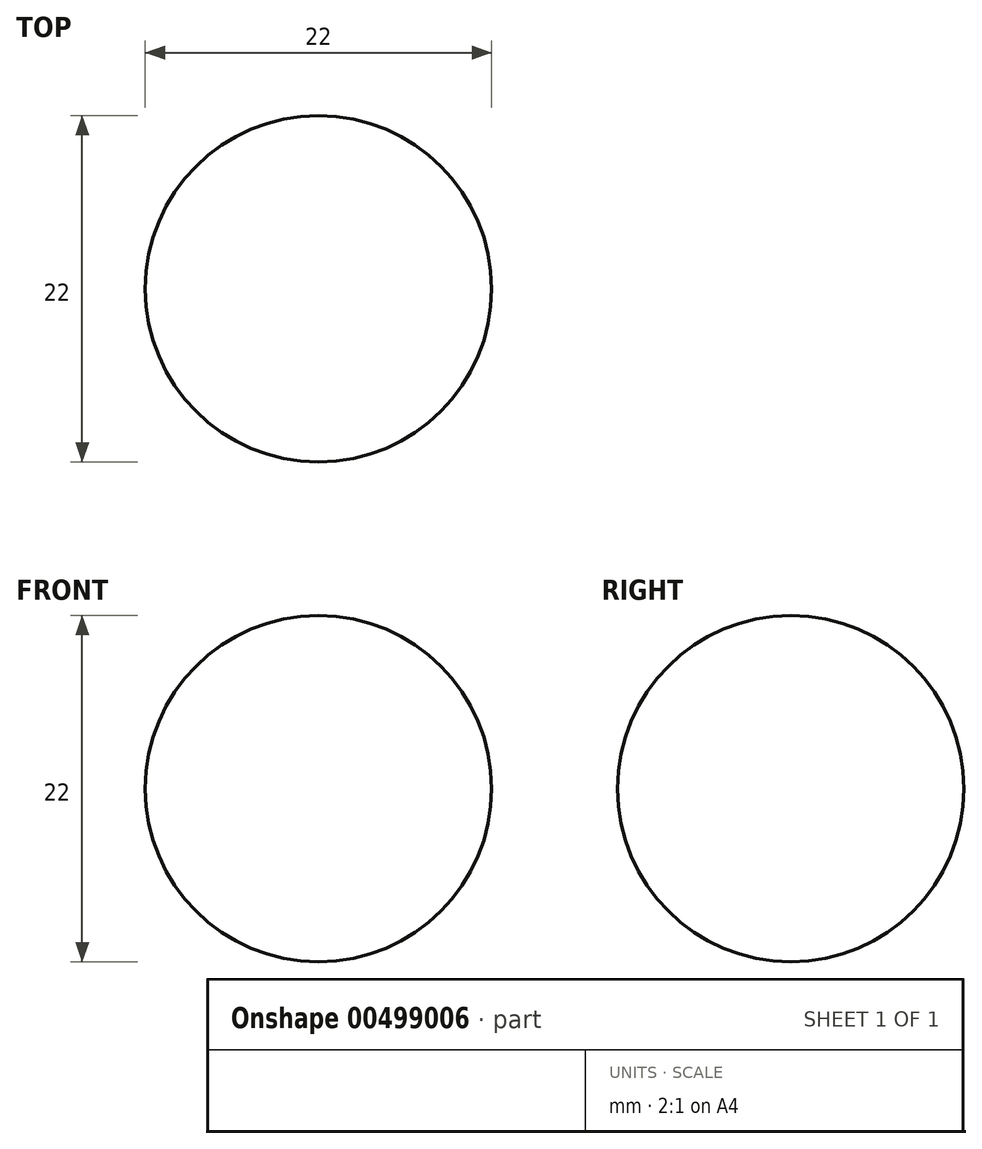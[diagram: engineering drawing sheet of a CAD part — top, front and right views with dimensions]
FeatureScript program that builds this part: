
annotation { "Feature Type Name" : "Feature", "Feature Type Description" : "" }
export const myFeature = defineFeature(function(context is Context, id is Id, definition is map)
    precondition{}
    {
        {
            var Q0;
            Q0=qCreatedBy(makeId("Top.planeOp"),FACE);
            var sketch = newSketch(context, id + "F0", { "sketchPlane" : qUnion([Q0])});
            skArc(sketch, "E0", {"start": v(0, 40) * mm, "mid": v(11, 51) * mm, "end": v(0, 62) * mm});
            skLineSegment(sketch, "E1", {"start": v(0, 62) * mm, "end": v(0, 40) * mm});
            skSolve(sketch);
        }
        {
            var Q0;
            Q0 = qSketchRegion(id + "F0", true);
            var Q1;
            Q1=sQuery(id+"F0.wireOp",EDGE,"E1");
            revolve(context, id + "F1", {"entities" : qUnion([Q0]), "axis" : qUnion([Q1]), "revolveType" : RevolveType.FULL});
        }
    });
